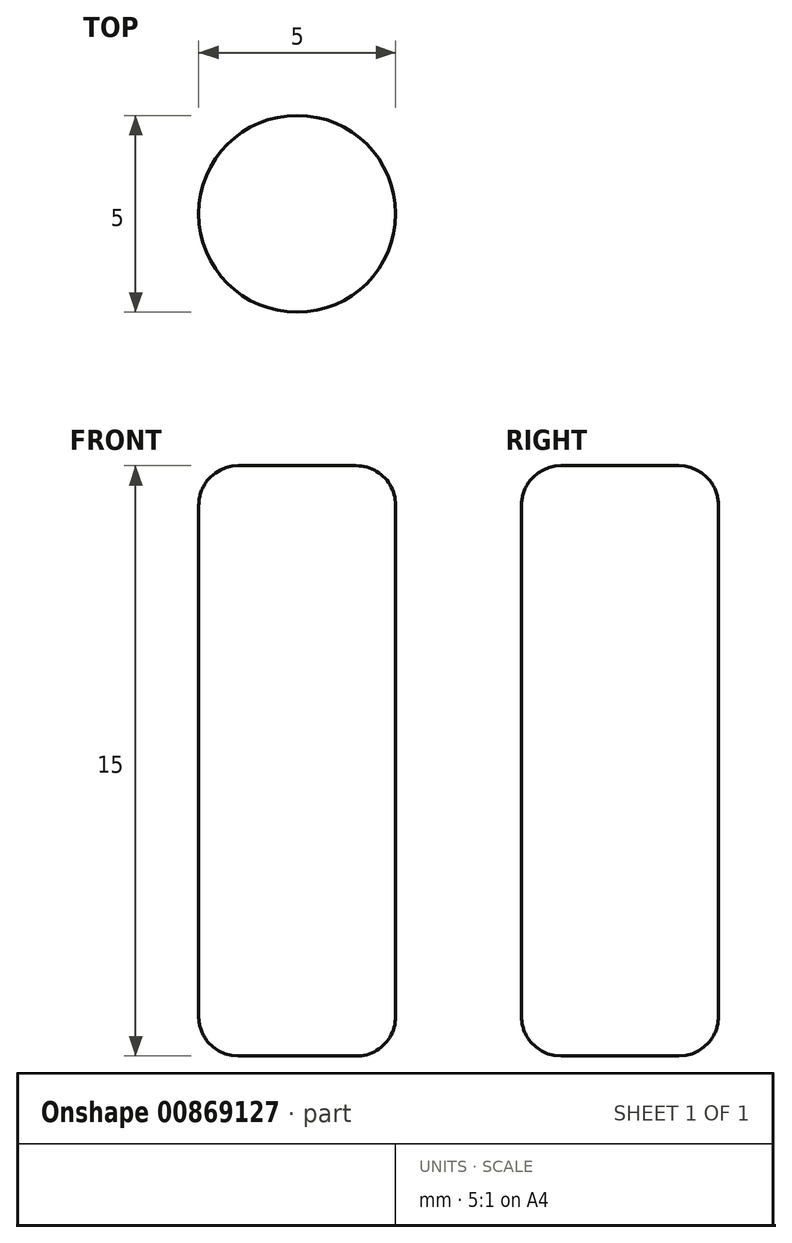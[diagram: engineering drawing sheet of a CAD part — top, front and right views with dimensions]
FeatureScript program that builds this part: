
annotation { "Feature Type Name" : "Feature", "Feature Type Description" : "" }
export const myFeature = defineFeature(function(context is Context, id is Id, definition is map)
    precondition{}
    {
        {
            var Q0;
            Q0=qCreatedBy(makeId("Top.planeOp"),FACE);
            var sketch = newSketch(context, id + "F0", { "sketchPlane" : qUnion([Q0]), "disableImprinting" : false});
            skCircle(sketch, "E0", {"center": v(0, 0) * mm, "radius": 2.5 * mm});
            skSolve(sketch);
        }
        {
            var Q0;
            Q0 = qSketchRegion(id + "F0", true);
            extrude(context, id + "F1", {"entities" : qUnion([Q0]), "flatOperationType" : FlatOperationType.REMOVE, "depth" : 15 * mm, "offsetDistance" : 25 * mm, "startOffsetBound" : StartOffsetType.BLIND, "startOffsetDistance" : 25 * mm, "symmetric" : true, "domain" : OperationDomain.MODEL});
        }
        {
            var Q0;
            Q0=makeQuery(id+"F1.opExtrude","SWEPT_FACE",FACE,{"disambiguationData":[OSD([sQuery(id+"F0.wireOp",EDGE,"E0")])]});
            fillet(context, id + "F2", {"entities" : qUnion([Q0]), "radius" : 1 * mm, "tangentPropagation" : true, "allowEdgeOverflow" : false});
        }
    });
